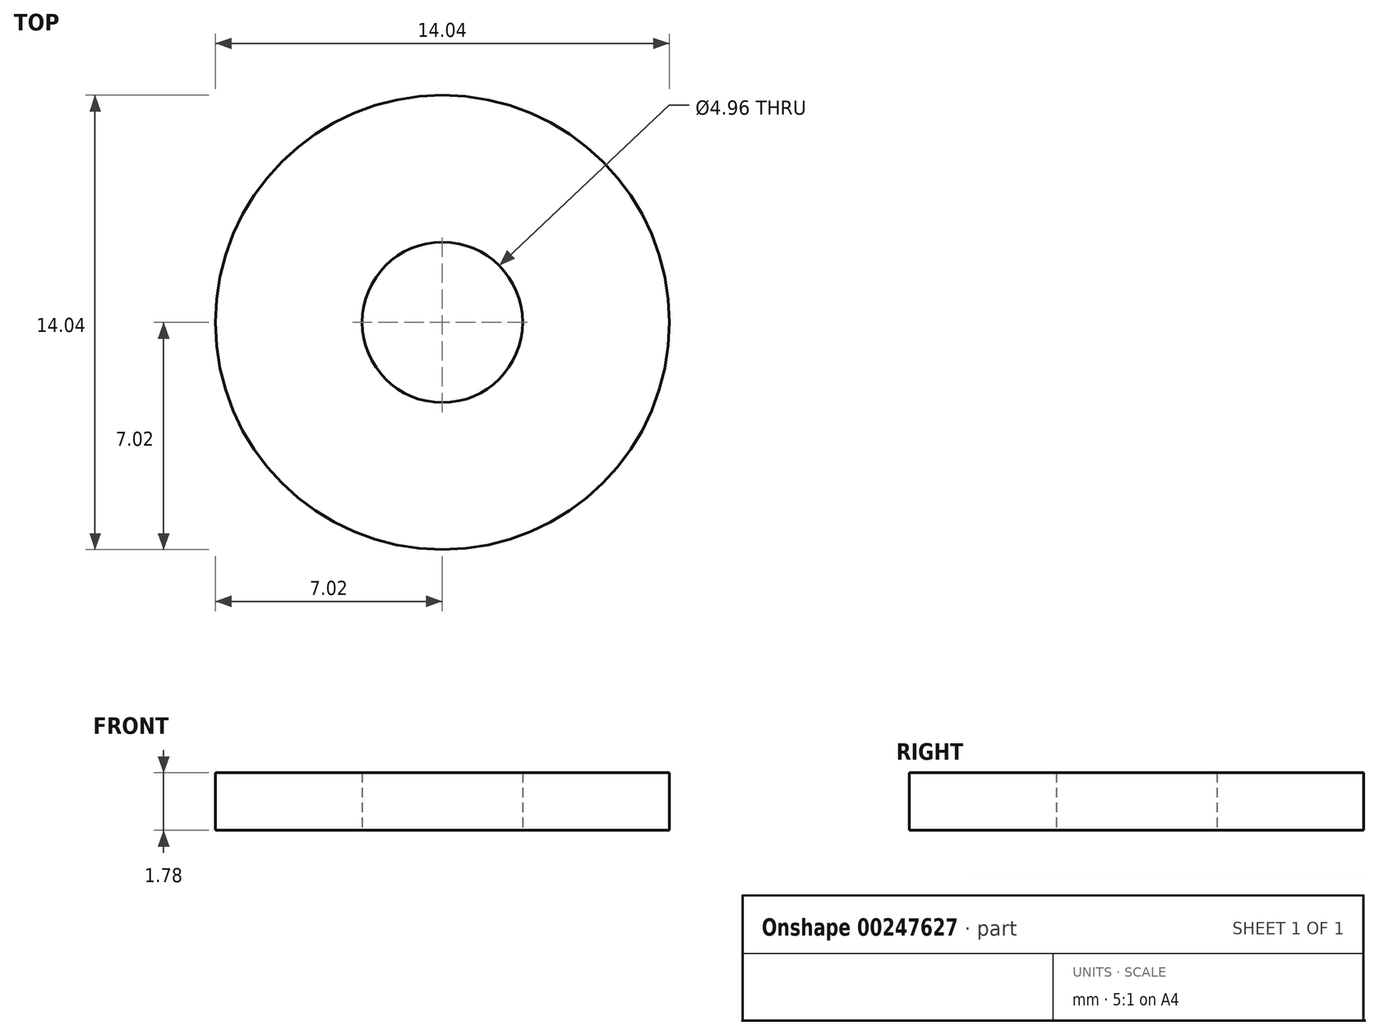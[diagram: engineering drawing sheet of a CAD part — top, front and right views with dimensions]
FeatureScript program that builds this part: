
annotation { "Feature Type Name" : "Feature", "Feature Type Description" : "" }
export const myFeature = defineFeature(function(context is Context, id is Id, definition is map)
    precondition{}
    {
        {
            var Q0;
            Q0=qCreatedBy(makeId("Top.planeOp"),FACE);
            var sketch = newSketch(context, id + "F0", { "sketchPlane" : qUnion([Q0])});
            skCircle(sketch, "E0", {"center": v(0, 0) * mm, "radius": 2.48 * mm});
            skCircle(sketch, "E1", {"center": v(0, 0) * mm, "radius": 7.02 * mm});
            skSolve(sketch);
        }
        {
            var Q0;
            Q0 = qSketchRegion(id + "F0", true);
            extrude(context, id + "F1", {"entities" : qUnion([Q0]), "depth" : 1.78 * mm});
        }
    });
